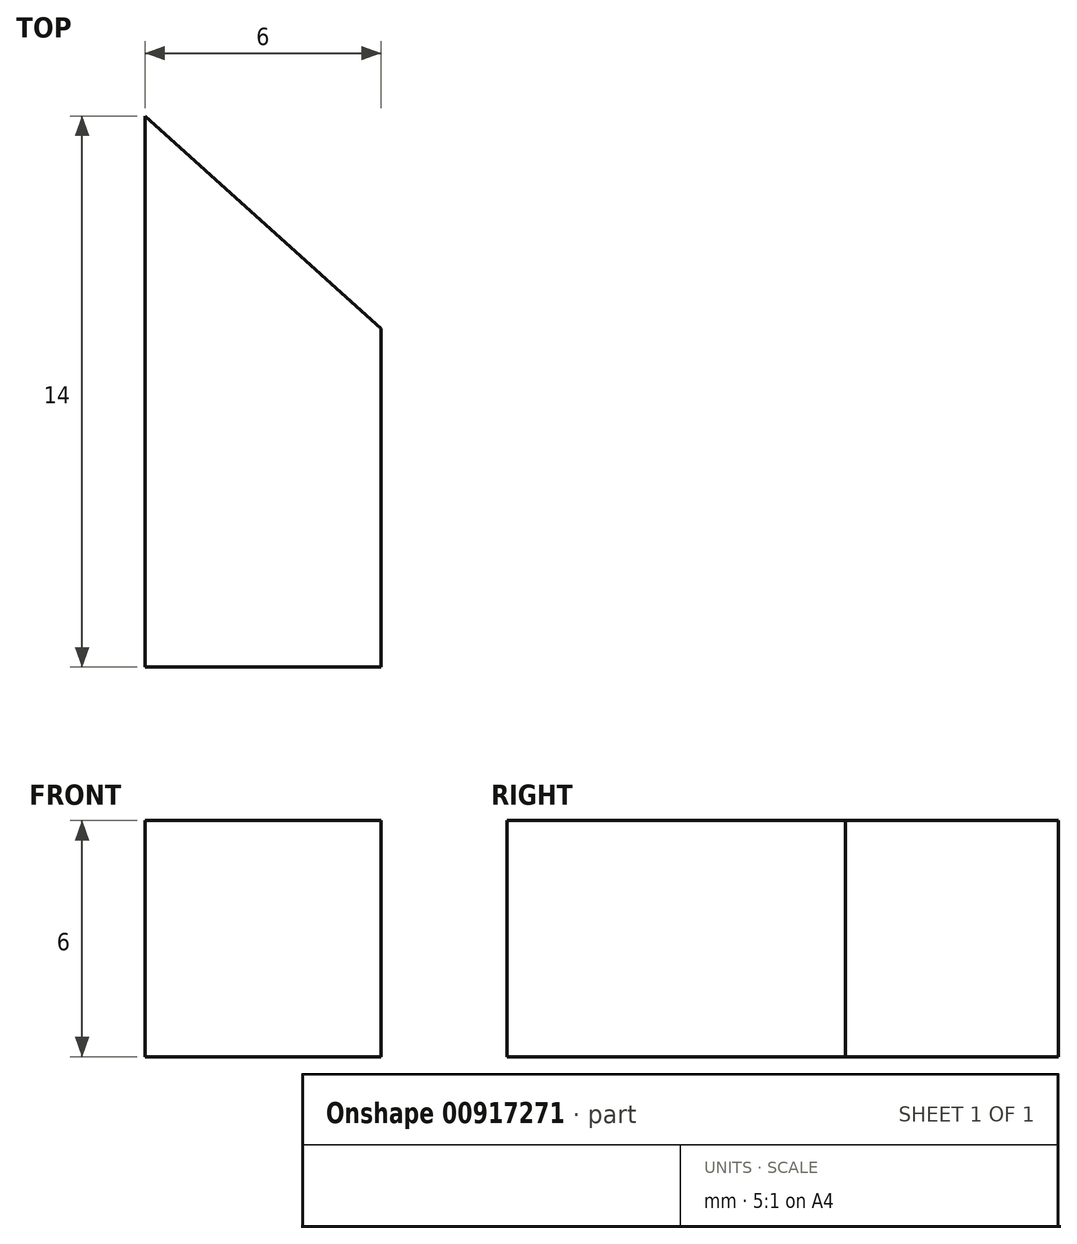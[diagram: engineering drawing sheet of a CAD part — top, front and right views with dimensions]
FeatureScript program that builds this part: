
annotation { "Feature Type Name" : "Feature", "Feature Type Description" : "" }
export const myFeature = defineFeature(function(context is Context, id is Id, definition is map)
    precondition{}
    {
        {
            var Q0;
            Q0=qCreatedBy(makeId("Front.planeOp"),FACE);
            var sketch = newSketch(context, id + "F0", { "sketchPlane" : qUnion([Q0])});
            skLineSegment(sketch, "E0.bottom", {"start": v(3, 3) * mm, "end": v(-3, 3) * mm});
            skLineSegment(sketch, "E0.top", {"start": v(3, -3) * mm, "end": v(-3, -3) * mm});
            skLineSegment(sketch, "E0.left", {"start": v(3, 3) * mm, "end": v(3, -3) * mm});
            skLineSegment(sketch, "E0.right", {"start": v(-3, 3) * mm, "end": v(-3, -3) * mm});
            skPoint(sketch, "E0.middle", {"position": v(0, 0) * mm});
            skSolve(sketch);
        }
        {
            var Q0;
            Q0=makeQuery(id+"F0.imprint","IMPRINT",FACE,{"disambiguationData":[TD([[makeQuery(id+"F0.imprint","IMPRINT",EDGE,{"derivedFrom":sQuery(id+"F0.wireOp",EDGE,"E0.bottom")}),1.0]])]});
            extrude(context, id + "F1", {"entities" : qUnion([Q0]), "depth" : 14 * mm, "offsetDistance" : 25 * mm});
        }
        {
            var Q0;
            Q0=makeQuery(id+"F1.opExtrude","SWEPT_FACE",FACE,{"disambiguationData":[OSD([sQuery(id+"F0.wireOp",EDGE,"E0.bottom")])]});
            var sketch = newSketch(context, id + "F2", { "sketchPlane" : qUnion([Q0])});
            skLineSegment(sketch, "E1", {"start": v(-3, 0) * mm, "end": v(3, -5.4) * mm});
            skSolve(sketch);
        }
        {
            var Q0;
            Q0 = qSketchRegion(id + "F2", true);
            var Q1;
            {var subQ0=sQuery(id+"F2.wireOp",EDGE,"E1");Q1=makeQuery(id+"F2.imprint","IMPRINT",FACE,{"disambiguationData":[TD([[makeQuery(id+"F2.imprint","IMPRINT",EDGE,{"derivedFrom":subQ0}),1.0]])]});}
            extrude(context, id + "F3", {"entities" : qUnion([Q0, Q1]), "operationType" : NewBodyOperationType.REMOVE, "endBound" : BoundingType.THROUGH_ALL, "oppositeDirection" : true, "depth" : 25 * mm, "offsetDistance" : 25 * mm});
        }
    });
